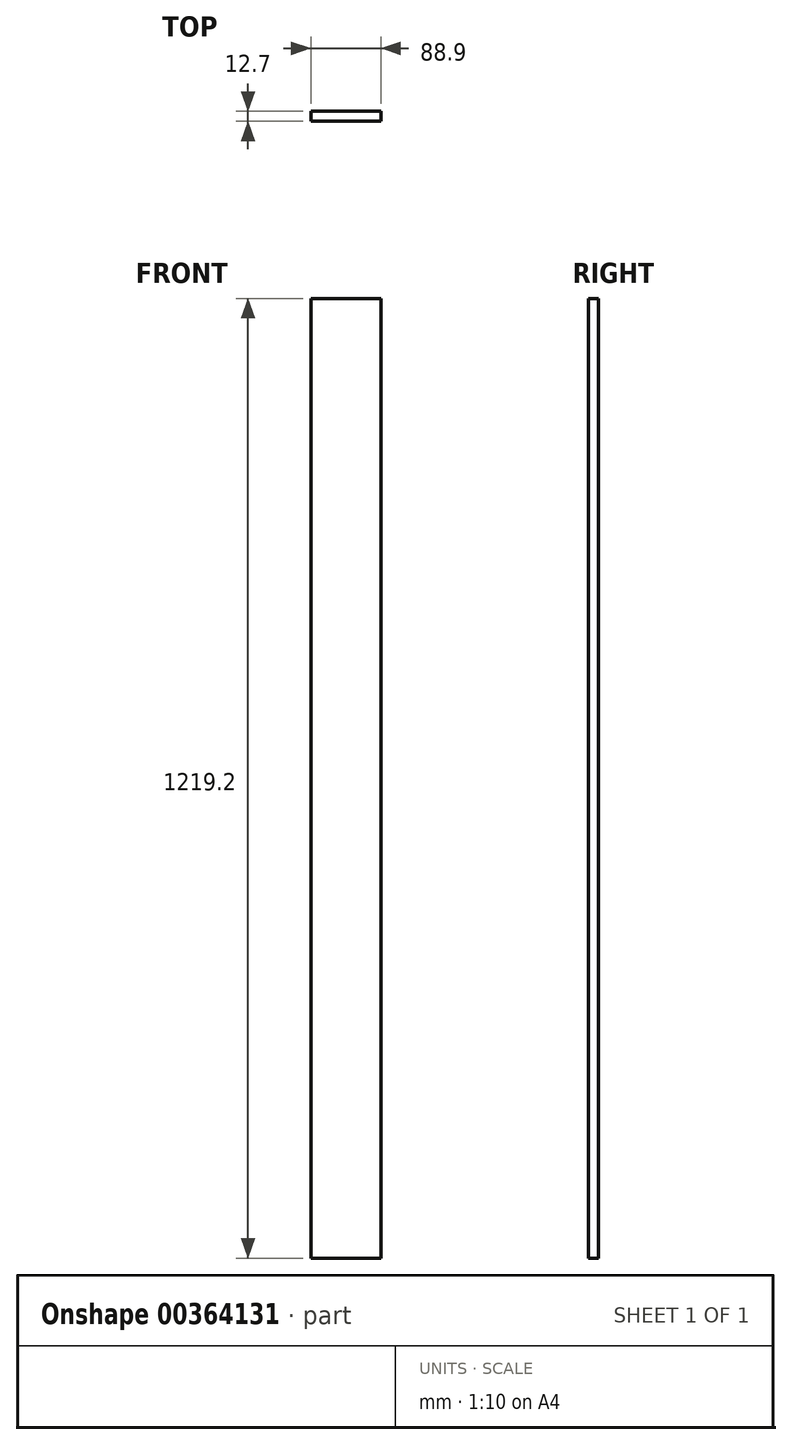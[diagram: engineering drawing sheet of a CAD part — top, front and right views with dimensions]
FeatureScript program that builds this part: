
annotation { "Feature Type Name" : "Feature", "Feature Type Description" : "" }
export const myFeature = defineFeature(function(context is Context, id is Id, definition is map)
    precondition{}
    {
        {
            var Q0;
            Q0=qCreatedBy(makeId("Front.planeOp"),FACE);
            var sketch = newSketch(context, id + "F0", { "sketchPlane" : qUnion([Q0])});
            skLineSegment(sketch, "E0.bottom", {"start": v(-52.38, 1138.1) * mm, "end": v(36.52, 1138.1) * mm});
            skLineSegment(sketch, "E0.top", {"start": v(-52.38, -81.1) * mm, "end": v(36.52, -81.1) * mm});
            skLineSegment(sketch, "E0.left", {"start": v(-52.38, 1138.1) * mm, "end": v(-52.38, -81.1) * mm});
            skLineSegment(sketch, "E0.right", {"start": v(36.52, 1138.1) * mm, "end": v(36.52, -81.1) * mm});
            skSolve(sketch);
        }
        {
            var Q0;
            Q0=makeQuery(id+"F0.imprint","IMPRINT",FACE,{"disambiguationData":[TD([[makeQuery(id+"F0.imprint","IMPRINT",EDGE,{"derivedFrom":sQuery(id+"F0.wireOp",EDGE,"E0.bottom")}),-1.0]])]});
            extrude(context, id + "F1", {"entities" : qUnion([Q0]), "depth" : 12.7 * mm});
        }
    });
